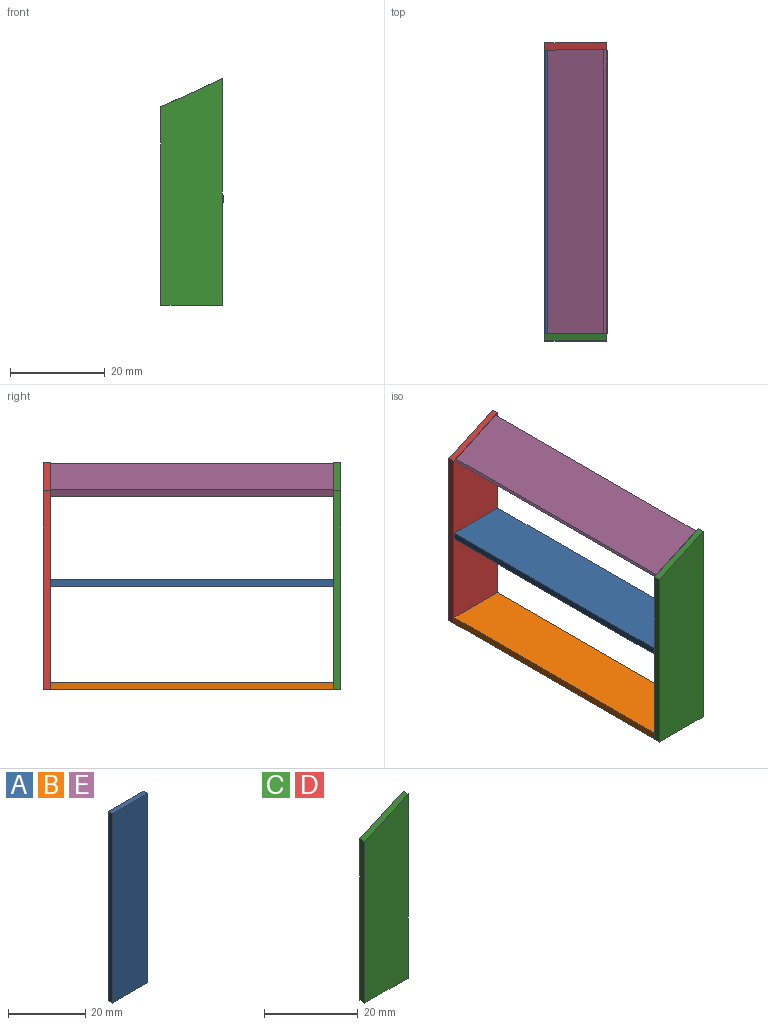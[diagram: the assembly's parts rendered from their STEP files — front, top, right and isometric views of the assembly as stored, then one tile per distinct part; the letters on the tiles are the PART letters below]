
ASSEMBLY  parts=5 mates=5
PART A: 6 faces, bbox 13x1.5x60 mm
  f0: plane 13x1.5mm, normal (0,0,-1), area 19.5mm2, adj f1,f3,f4,f5
  f1: plane 60x1.5mm, normal (1,0,0), area 90mm2, adj f0,f2,f4,f5
  f2: plane 13x1.5mm, normal (0,0,1), area 19.5mm2, adj f1,f3,f4,f5
  f3: plane 60x1.5mm, normal (-1,0,0), area 90mm2, adj f0,f2,f4,f5
  f4: plane 60x13mm, normal (0,-1,0), area 780mm2, adj f0,f1,f2,f3
  f5: plane 60x13mm, normal (0,1,0), area 780mm2, adj f0,f1,f2,f3
PART B: same geometry as A
PART C: 6 faces, bbox 13x1.5x48 mm
  f0: plane 13x1.5mm, normal (0,0,-1), area 19.5mm2, adj f1,f3,f4,f5
  f1: plane 48x1.5mm, normal (1,0,0), area 72mm2, adj f0,f2,f4,f5
  f2: plane 13x6mm, normal (-0.42,0,0.91), area 21.5mm2, adj f1,f3,f4,f5
  f3: plane 42x1.5mm, normal (-1,0,0), area 63mm2, adj f0,f2,f4,f5
  f4: plane 48x13mm, normal (0,-1,0), area 585mm2, adj f0,f1,f2,f3
  f5: plane 48x13mm, normal (0,1,0), area 585mm2, adj f0,f1,f2,f3
PART D: same geometry as C
PART E: same geometry as A
PLACE A rot(axis=(-1,0,0),90deg) t=(41.1,-36.67,-4.22)mm
PLACE B rot(axis=(1,0,0),90deg) t=(40.95,-24.83,-24.5)mm
PLACE C t=(0,-61.5,0)mm
PLACE D at identity
PLACE E rot(axis=(0.95,-0.21,0.21),92.6deg) t=(37.18,-24.83,36.16)mm
MATE cylindrical E.f0 <-> D.f4  axis (0,1,0) through (0,-0.75,19)mm
MATE fastened D.f4 <-> A.f2  axis (0,-1,0) through (0.14,-0.75,-3.47)mm
MATE fastened B.f0 <-> D.f4  axis (0,1,0) through (0,-0.75,-26)mm
MATE planar E.f5 <-> C.f2  axis (-0.42,0,0.91) through (0,-30.75,19)mm
MATE fastened C.f5 <-> B.f2  axis (0,1,0) through (0,-60.75,-26)mm
